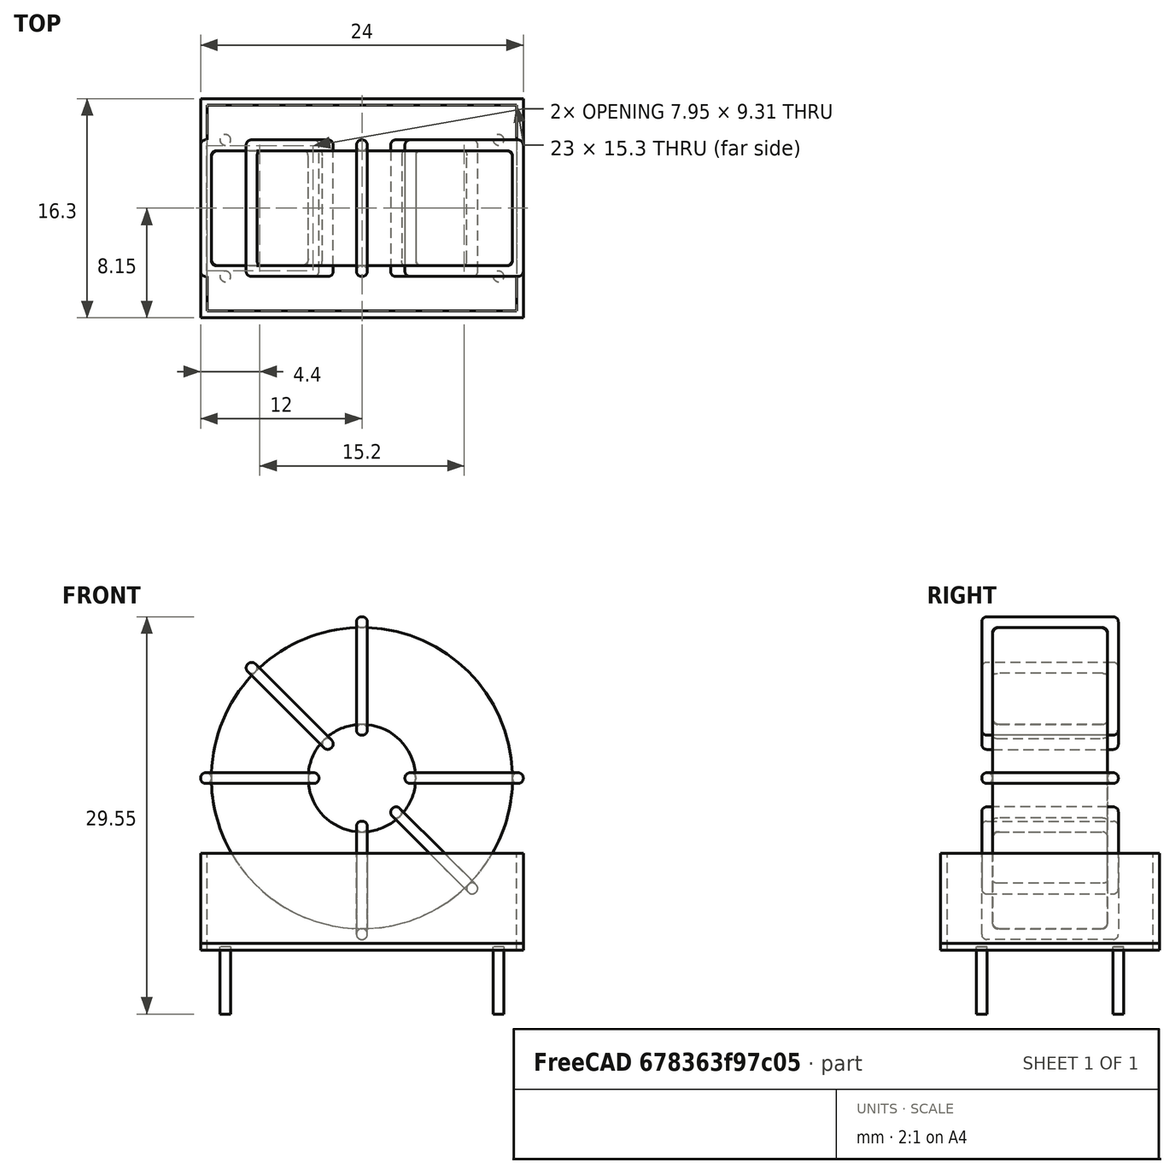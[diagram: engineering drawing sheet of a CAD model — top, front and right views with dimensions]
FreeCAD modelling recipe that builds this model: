
FCSTD DOCUMENT  (FreeCAD 0.16R6703 (Git))
Label: L_Radial_round_toroid_vertical_box_4pin_master
License: All rights reserved
LicenseURL: http://en.wikipedia.org/wiki/All_rights_reserved
objects: Sketcher::SketchObject×8, PartDesign::Pad×8, PartDesign::Fillet×5, Spreadsheet::Sheet×1
note: 29 computed .brp shape members not serialized (recipe doc carries the construction recipe); baked Part::Feature solids carry a one-line shape summary decoded from their .brp

FEATURE [Spreadsheet::Sheet] Spreadsheet  label="dimensions"
  cells = A1=Wx; B1(Wx)=24; C1(WW)=8; D1(iWx)=24; A2=Wy; B2(Wy)=10.16; D2(iWy)=16.3; A3=RM; B3(RMx)=10.16; C3(RMy)=20.32; A4=d_wire; B4(d_wire)=0.8; A5=H; B5(H)=31; A6=offsetx; B6(offsetx)=1.84
FEATURE [Sketcher::SketchObject] Sketch
  Placement = pos=(10.16,-5.08,0) rot=(1,0,0;1.5708rad)
  expr: Placement.Base.x = Spreadsheet.RMy / 2
  expr: Constraints[4] = Spreadsheet.WW / 2
  expr: Placement.Base.y = -Spreadsheet.RMx / 2
  expr: Constraints[0] = Spreadsheet.Wx / 2 - Spreadsheet.d_wire
  expr: Constraints[2] = Spreadsheet.Wx / 2 + Spreadsheet.d_wire + 0.5
  sketch-geometry (2):
    g0: Circle CenterX=0 CenterY=13.3 CenterZ=0 NormalX=0 NormalY=0 NormalZ=1 Radius=11.2
    g1: Circle CenterX=0 CenterY=13.3 CenterZ=0 NormalX=0 NormalY=0 NormalZ=1 Radius=4
  constraints (5):
    c: Radius(g0) = 11.2
    c: DistanceX(g-1,g0) = 0
    c: DistanceY(g-1,g0) = 13.3
    c: Coincident(g1,g0)
    c: Radius(g1) = 4
FEATURE [PartDesign::Pad] Pad
  Length = 8.56
  Length2 = 100
  Midplane = true
  Placement = pos=(10.16,-5.08,0) rot=(1,0,0;1.5708rad)
  Sketch = -> Sketch
  Type = 0
  expr: Length = Spreadsheet.Wy - 2 * Spreadsheet.d_wire
FEATURE [Sketcher::SketchObject] Sketch001
  Placement = pos=(0,0,0.75) rot=(0,0,1;0rad)
  expr: Constraints[4] = Spreadsheet.RMy
  expr: Constraints[2] = -Spreadsheet.RMx
  expr: Constraints[1] = Spreadsheet.d_wire / 2
  sketch-geometry (4):
    g0: Circle CenterX=0 CenterY=0 CenterZ=0 NormalX=0 NormalY=0 NormalZ=1 Radius=0.4
    g1: Circle CenterX=20.32 CenterY=-10.16 CenterZ=0 NormalX=0 NormalY=0 NormalZ=1 Radius=0.4
    g2: Circle CenterX=0 CenterY=-10.16 CenterZ=0 NormalX=0 NormalY=0 NormalZ=1 Radius=0.4
    g3: Circle CenterX=20.32 CenterY=0 CenterZ=0 NormalX=0 NormalY=0 NormalZ=1 Radius=0.4
  constraints (11):
    c: Equal(g0,g1)
    c: Radius(g0) = 0.4
    c: DistanceY(g-1,g1) = -10.16
    c: Coincident(g0,g-1)
    c: DistanceX(g-1,g1) = 20.32
    c: PointOnObject(g2,g-2)
    c: DistanceY(g-1,g3) = 0
    c: DistanceY(g2,g1) = 0
    c: DistanceX(g3,g1) = 0
    c: Equal(g3,g2)
    c: Equal(g2,g1)
FEATURE [PartDesign::Pad] Pad001
  Length = 5
  Length2 = 0
  Placement = pos=(0,0,0.75) rot=(0,0,1;0rad)
  Reversed = true
  Sketch = -> Sketch001
  Type = 0
FEATURE [PartDesign::Fillet] Fillet
  Base = -> Pad [Edge6,Edge3,Edge2]
  Placement = pos=(10.16,-5.08,0) rot=(1,0,0;1.5708rad)
  Radius = 0.5
FEATURE [Sketcher::SketchObject] Sketch003
  Placement = pos=(10.16,0,13.3) rot=(1,0,0;3.14159rad)
  expr: Placement.Base.x = Spreadsheet.RMy / 2
  expr: Constraints[18] = Spreadsheet.d_wire
  expr: Constraints[16] = Spreadsheet.d_wire
  expr: Constraints[19] = Spreadsheet.d_wire
  expr: Constraints[17] = Spreadsheet.d_wire
  expr: Placement.Base.y = -1 * (Spreadsheet.RMx - Spreadsheet.Wy) / 2
  expr: Constraints[21] = (Spreadsheet.Wx - Spreadsheet.WW) / 2 - Spreadsheet.d_wire
  expr: Constraints[22] = Spreadsheet.Wx / 2 - Spreadsheet.d_wire
  expr: Constraints[43] = Spreadsheet.d_wire
  expr: Constraints[48] = Spreadsheet.Wx - Spreadsheet.d_wire * 2
  expr: Constraints[49] = Spreadsheet.Wy
  expr: Placement.Base.z = Spreadsheet.Wx / 2 + Spreadsheet.d_wire + 0.5
  sketch-geometry (16):
    g0: LineSegment StartX=-3.2 StartY=0 StartZ=0 EndX=-12 EndY=0 EndZ=0
    g1: LineSegment StartX=-12 StartY=0 StartZ=0 EndX=-12 EndY=10.16 EndZ=0
    g2: LineSegment StartX=-12 StartY=10.16 StartZ=0 EndX=-3.2 EndY=10.16 EndZ=0
    g3: LineSegment StartX=-3.2 StartY=10.16 StartZ=0 EndX=-3.2 EndY=0 EndZ=0
    g4: LineSegment StartX=-11.2 StartY=9.36 StartZ=0 EndX=-4 EndY=9.36 EndZ=0
    g5: LineSegment StartX=-4 StartY=9.36 StartZ=0 EndX=-4 EndY=0.8 EndZ=0
    g6: LineSegment StartX=-4 StartY=0.8 StartZ=0 EndX=-11.2 EndY=0.8 EndZ=0
    g7: LineSegment StartX=-11.2 StartY=0.8 StartZ=0 EndX=-11.2 EndY=9.36 EndZ=0
    g8: LineSegment StartX=3.2 StartY=10.16 StartZ=0 EndX=12 EndY=10.16 EndZ=0
    g9: LineSegment StartX=12 StartY=10.16 StartZ=0 EndX=12 EndY=0 EndZ=0
    g10: LineSegment StartX=12 StartY=0 StartZ=0 EndX=3.2 EndY=0 EndZ=0
    g11: LineSegment StartX=3.2 StartY=0 StartZ=0 EndX=3.2 EndY=10.16 EndZ=0
    g12: LineSegment StartX=4 StartY=9.36 StartZ=0 EndX=11.2 EndY=9.36 EndZ=0
    g13: LineSegment StartX=11.2 StartY=9.36 StartZ=0 EndX=11.2 EndY=0.8 EndZ=0
    g14: LineSegment StartX=11.2 StartY=0.8 StartZ=0 EndX=4 EndY=0.8 EndZ=0
    g15: LineSegment StartX=4 StartY=0.8 StartZ=0 EndX=4 EndY=9.36 EndZ=0
  constraints (50):
    c: Horizontal(g0)
    c: Coincident(g1,g0)
    c: Vertical(g1)
    c: Coincident(g2,g1)
    c: Horizontal(g2)
    c: Coincident(g3,g2)
    c: Coincident(g3,g0)
    c: Vertical(g3)
    c: Coincident(g4,g5)
    c: Coincident(g5,g6)
    c: Coincident(g6,g7)
    c: Coincident(g7,g4)
    c: Horizontal(g4)
    c: Horizontal(g6)
    c: Vertical(g5)
    c: Vertical(g7)
    c: DistanceX(g1,g4) = 0.8
    c: DistanceY(g4,g1) = 0.8
    c: DistanceX(g5,g0) = 0.8
    c: DistanceY(g0,g5) = 0.8
    c: DistanceY(g-1,g0) = 0
    c: DistanceX(g6,g6) = 7.2
    c: DistanceX(g6,g-1) = 11.2
    c: Coincident(g8,g9)
    c: Coincident(g9,g10)
    c: Coincident(g10,g11)
    c: Coincident(g11,g8)
    c: Horizontal(g8)
    c: Horizontal(g10)
    c: Vertical(g9)
    c: Vertical(g11)
    c: Coincident(g12,g13)
    c: Coincident(g13,g14)
    c: Coincident(g14,g15)
    c: Coincident(g15,g12)
    c: Horizontal(g12)
    c: Horizontal(g14)
    c: Vertical(g13)
    c: Vertical(g15)
    c: DistanceY(g8,g2) = 0
    c: DistanceY(g10,g0) = 0
    c: DistanceY(g14,g5) = 0
    c: DistanceY(g12,g4) = 0
    c: DistanceX(g8,g12) = 0.8
    c: Equal(g8,g2)
    c: Equal(g12,g4)
    c: Equal(g9,g1)
    c: Equal(g13,g7)
    c: DistanceX(g4,g12) = 22.4
    c: DistanceY(g0,g1) = 10.16
FEATURE [PartDesign::Pad] Pad002
  Length = 0.8
  Length2 = 100
  Midplane = true
  Placement = pos=(10.16,0,13.3) rot=(1,0,0;3.14159rad)
  Sketch = -> Sketch003
  Type = 0
  expr: Length = Spreadsheet.d_wire
FEATURE [PartDesign::Fillet] Fillet001
  Base = -> Pad002 [Edge38,Edge41,Edge42,Edge43,Edge29,Edge32,Edge33,Edge34,Edge25,Edge35,Edge36,Edge13,Edge14,Edge15,Edge16,Edge17,Edge18,Edge19,Edge1,Edge2,Edge3,Edge4,Edge5,Edge6,Edge7,Edge37,Edge39,Edge40,Edge20,Edge23,Edge24,Edge21,Edge22,Edge8,Edge9,Edge10,Edge11,Edge12,Edge26,Edge27,+8 more]
  Placement = pos=(10.16,0,13.3) rot=(1,0,0;3.14159rad)
  Radius = 0.376
  expr: Radius = Spreadsheet.d_wire * 0.47
FEATURE [Sketcher::SketchObject] Sketch004
  Placement = pos=(10.16,0,13.3) rot=(0.92388,0,0.382683;3.14159rad)
  expr: Placement.Base.x = Spreadsheet.RMy / 2
  expr: Constraints[18] = Spreadsheet.d_wire
  expr: Constraints[16] = Spreadsheet.d_wire
  expr: Constraints[19] = Spreadsheet.d_wire
  expr: Constraints[17] = Spreadsheet.d_wire
  expr: Placement.Base.y = -1 * (Spreadsheet.RMx - Spreadsheet.Wy) / 2
  expr: Constraints[21] = (Spreadsheet.Wx - Spreadsheet.WW) / 2 - Spreadsheet.d_wire
  expr: Constraints[22] = Spreadsheet.Wx / 2 - Spreadsheet.d_wire
  expr: Constraints[43] = Spreadsheet.d_wire
  expr: Constraints[48] = Spreadsheet.Wx - 2 * Spreadsheet.d_wire
  expr: Constraints[49] = Spreadsheet.Wy
  expr: Placement.Base.z = Spreadsheet.Wx / 2 + Spreadsheet.d_wire + 0.5
  sketch-geometry (16):
    g0: LineSegment StartX=-3.2 StartY=0 StartZ=0 EndX=-12 EndY=0 EndZ=0
    g1: LineSegment StartX=-12 StartY=0 StartZ=0 EndX=-12 EndY=10.16 EndZ=0
    g2: LineSegment StartX=-12 StartY=10.16 StartZ=0 EndX=-3.2 EndY=10.16 EndZ=0
    g3: LineSegment StartX=-3.2 StartY=10.16 StartZ=0 EndX=-3.2 EndY=0 EndZ=0
    g4: LineSegment StartX=-11.2 StartY=9.36 StartZ=0 EndX=-4 EndY=9.36 EndZ=0
    g5: LineSegment StartX=-4 StartY=9.36 StartZ=0 EndX=-4 EndY=0.8 EndZ=0
    g6: LineSegment StartX=-4 StartY=0.8 StartZ=0 EndX=-11.2 EndY=0.8 EndZ=0
    g7: LineSegment StartX=-11.2 StartY=0.8 StartZ=0 EndX=-11.2 EndY=9.36 EndZ=0
    g8: LineSegment StartX=3.2 StartY=10.16 StartZ=0 EndX=12 EndY=10.16 EndZ=0
    g9: LineSegment StartX=12 StartY=10.16 StartZ=0 EndX=12 EndY=0 EndZ=0
    g10: LineSegment StartX=12 StartY=0 StartZ=0 EndX=3.2 EndY=0 EndZ=0
    g11: LineSegment StartX=3.2 StartY=0 StartZ=0 EndX=3.2 EndY=10.16 EndZ=0
    g12: LineSegment StartX=4 StartY=9.36 StartZ=0 EndX=11.2 EndY=9.36 EndZ=0
    g13: LineSegment StartX=11.2 StartY=9.36 StartZ=0 EndX=11.2 EndY=0.8 EndZ=0
    g14: LineSegment StartX=11.2 StartY=0.8 StartZ=0 EndX=4 EndY=0.8 EndZ=0
    g15: LineSegment StartX=4 StartY=0.8 StartZ=0 EndX=4 EndY=9.36 EndZ=0
  constraints (50):
    c: Horizontal(g0)
    c: Coincident(g1,g0)
    c: Vertical(g1)
    c: Coincident(g2,g1)
    c: Horizontal(g2)
    c: Coincident(g3,g2)
    c: Coincident(g3,g0)
    c: Vertical(g3)
    c: Coincident(g4,g5)
    c: Coincident(g5,g6)
    c: Coincident(g6,g7)
    c: Coincident(g7,g4)
    c: Horizontal(g4)
    c: Horizontal(g6)
    c: Vertical(g5)
    c: Vertical(g7)
    c: DistanceX(g1,g4) = 0.8
    c: DistanceY(g4,g1) = 0.8
    c: DistanceX(g5,g0) = 0.8
    c: DistanceY(g0,g5) = 0.8
    c: DistanceY(g-1,g0) = 0
    c: DistanceX(g6,g6) = 7.2
    c: DistanceX(g6,g-1) = 11.2
    c: Coincident(g8,g9)
    c: Coincident(g9,g10)
    c: Coincident(g10,g11)
    c: Coincident(g11,g8)
    c: Horizontal(g8)
    c: Horizontal(g10)
    c: Vertical(g9)
    c: Vertical(g11)
    c: Coincident(g12,g13)
    c: Coincident(g13,g14)
    c: Coincident(g14,g15)
    c: Coincident(g15,g12)
    c: Horizontal(g12)
    c: Horizontal(g14)
    c: Vertical(g13)
    c: Vertical(g15)
    c: DistanceY(g8,g2) = 0
    c: DistanceY(g10,g0) = 0
    c: DistanceY(g14,g5) = 0
    c: DistanceY(g12,g4) = 0
    c: DistanceX(g8,g12) = 0.8
    c: Equal(g8,g2)
    c: Equal(g12,g4)
    c: Equal(g9,g1)
    c: Equal(g13,g7)
    c: DistanceX(g4,g12) = 22.4
    c: DistanceY(g0,g1) = 10.16
FEATURE [PartDesign::Pad] Pad003
  Length = 0.8
  Length2 = 100
  Midplane = true
  Placement = pos=(10.16,0,13.3) rot=(0.92388,0,0.382683;3.14159rad)
  Sketch = -> Sketch004
  Type = 0
  expr: Length = Spreadsheet.d_wire
FEATURE [PartDesign::Fillet] Fillet002
  Base = -> Pad003 [Edge38,Edge41,Edge42,Edge43,Edge29,Edge32,Edge33,Edge34,Edge25,Edge35,Edge36,Edge13,Edge14,Edge15,Edge16,Edge17,Edge18,Edge19,Edge1,Edge2,Edge3,Edge4,Edge5,Edge6,Edge7,Edge37,Edge39,Edge40,Edge20,Edge23,Edge24,Edge21,Edge22,Edge8,Edge9,Edge10,Edge11,Edge12,Edge26,Edge27,+8 more]
  Placement = pos=(10.16,0,13.3) rot=(0.92388,0,0.382683;3.14159rad)
  Radius = 0.376
  expr: Radius = Spreadsheet.d_wire * 0.47
FEATURE [Sketcher::SketchObject] Sketch005
  Placement = pos=(10.16,0,13.3) rot=(0.92388,0,-0.382683;3.14159rad)
  expr: Placement.Base.x = Spreadsheet.RMy / 2
  expr: Constraints[18] = Spreadsheet.d_wire
  expr: Constraints[16] = Spreadsheet.d_wire
  expr: Constraints[19] = Spreadsheet.d_wire
  expr: Constraints[17] = Spreadsheet.d_wire
  expr: Placement.Base.y = -1 * (Spreadsheet.RMx - Spreadsheet.Wy) / 2
  expr: Constraints[21] = (Spreadsheet.Wx - Spreadsheet.WW) / 2 - Spreadsheet.d_wire
  expr: Constraints[22] = Spreadsheet.Wx / 2 - Spreadsheet.d_wire
  expr: Constraints[43] = Spreadsheet.d_wire
  expr: Constraints[48] = Spreadsheet.Wx - 2 * Spreadsheet.d_wire
  expr: Constraints[49] = Spreadsheet.Wy
  expr: Placement.Base.z = Spreadsheet.Wx / 2 + Spreadsheet.d_wire + 0.5
  sketch-geometry (16):
    g0: LineSegment StartX=-3.2 StartY=0 StartZ=0 EndX=-12 EndY=0 EndZ=0
    g1: LineSegment StartX=-12 StartY=0 StartZ=0 EndX=-12 EndY=10.16 EndZ=0
    g2: LineSegment StartX=-12 StartY=10.16 StartZ=0 EndX=-3.2 EndY=10.16 EndZ=0
    g3: LineSegment StartX=-3.2 StartY=10.16 StartZ=0 EndX=-3.2 EndY=0 EndZ=0
    g4: LineSegment StartX=-11.2 StartY=9.36 StartZ=0 EndX=-4 EndY=9.36 EndZ=0
    g5: LineSegment StartX=-4 StartY=9.36 StartZ=0 EndX=-4 EndY=0.8 EndZ=0
    g6: LineSegment StartX=-4 StartY=0.8 StartZ=0 EndX=-11.2 EndY=0.8 EndZ=0
    g7: LineSegment StartX=-11.2 StartY=0.8 StartZ=0 EndX=-11.2 EndY=9.36 EndZ=0
    g8: LineSegment StartX=3.2 StartY=10.16 StartZ=0 EndX=12 EndY=10.16 EndZ=0
    g9: LineSegment StartX=12 StartY=10.16 StartZ=0 EndX=12 EndY=0 EndZ=0
    g10: LineSegment StartX=12 StartY=0 StartZ=0 EndX=3.2 EndY=0 EndZ=0
    g11: LineSegment StartX=3.2 StartY=0 StartZ=0 EndX=3.2 EndY=10.16 EndZ=0
    g12: LineSegment StartX=4 StartY=9.36 StartZ=0 EndX=11.2 EndY=9.36 EndZ=0
    g13: LineSegment StartX=11.2 StartY=9.36 StartZ=0 EndX=11.2 EndY=0.8 EndZ=0
    g14: LineSegment StartX=11.2 StartY=0.8 StartZ=0 EndX=4 EndY=0.8 EndZ=0
    g15: LineSegment StartX=4 StartY=0.8 StartZ=0 EndX=4 EndY=9.36 EndZ=0
  constraints (50):
    c: Horizontal(g0)
    c: Coincident(g1,g0)
    c: Vertical(g1)
    c: Coincident(g2,g1)
    c: Horizontal(g2)
    c: Coincident(g3,g2)
    c: Coincident(g3,g0)
    c: Vertical(g3)
    c: Coincident(g4,g5)
    c: Coincident(g5,g6)
    c: Coincident(g6,g7)
    c: Coincident(g7,g4)
    c: Horizontal(g4)
    c: Horizontal(g6)
    c: Vertical(g5)
    c: Vertical(g7)
    c: DistanceX(g1,g4) = 0.8
    c: DistanceY(g4,g1) = 0.8
    c: DistanceX(g5,g0) = 0.8
    c: DistanceY(g0,g5) = 0.8
    c: DistanceY(g-1,g0) = 0
    c: DistanceX(g6,g6) = 7.2
    c: DistanceX(g6,g-1) = 11.2
    c: Coincident(g8,g9)
    c: Coincident(g9,g10)
    c: Coincident(g10,g11)
    c: Coincident(g11,g8)
    c: Horizontal(g8)
    c: Horizontal(g10)
    c: Vertical(g9)
    c: Vertical(g11)
    c: Coincident(g12,g13)
    c: Coincident(g13,g14)
    c: Coincident(g14,g15)
    c: Coincident(g15,g12)
    c: Horizontal(g12)
    c: Horizontal(g14)
    c: Vertical(g13)
    c: Vertical(g15)
    c: DistanceY(g8,g2) = 0
    c: DistanceY(g10,g0) = 0
    c: DistanceY(g14,g5) = 0
    c: DistanceY(g12,g4) = 0
    c: DistanceX(g8,g12) = 0.8
    c: Equal(g8,g2)
    c: Equal(g12,g4)
    c: Equal(g9,g1)
    c: Equal(g13,g7)
    c: DistanceX(g4,g12) = 22.4
    c: DistanceY(g0,g1) = 10.16
FEATURE [PartDesign::Pad] Pad004
  Length = 0.8
  Length2 = 100
  Midplane = true
  Placement = pos=(10.16,0,13.3) rot=(0.92388,0,-0.382683;3.14159rad)
  Sketch = -> Sketch005
  Type = 0
  expr: Length = Spreadsheet.d_wire
FEATURE [PartDesign::Fillet] Fillet003
  Base = -> Pad004 [Edge38,Edge41,Edge42,Edge43,Edge29,Edge32,Edge33,Edge34,Edge25,Edge35,Edge36,Edge13,Edge14,Edge15,Edge16,Edge17,Edge18,Edge19,Edge1,Edge2,Edge3,Edge4,Edge5,Edge6,Edge7,Edge37,Edge39,Edge40,Edge20,Edge23,Edge24,Edge21,Edge22,Edge8,Edge9,Edge10,Edge11,Edge12,Edge26,Edge27,+8 more]
  Placement = pos=(10.16,0,13.3) rot=(0.92388,0,-0.382683;3.14159rad)
  Radius = 0.376
  expr: Radius = Spreadsheet.d_wire * 0.47
FEATURE [Sketcher::SketchObject] Sketch006
  Placement = pos=(10.16,0,13.3) rot=(0.707107,0,0.707107;3.14159rad)
  expr: Placement.Base.x = Spreadsheet.RMy / 2
  expr: Constraints[18] = Spreadsheet.d_wire
  expr: Constraints[16] = Spreadsheet.d_wire
  expr: Constraints[19] = Spreadsheet.d_wire
  expr: Constraints[17] = Spreadsheet.d_wire
  expr: Placement.Base.y = -1 * (Spreadsheet.RMx - Spreadsheet.Wy) / 2
  expr: Constraints[21] = (Spreadsheet.Wx - Spreadsheet.WW) / 2 - Spreadsheet.d_wire
  expr: Constraints[22] = Spreadsheet.Wx / 2 - Spreadsheet.d_wire
  expr: Constraints[43] = Spreadsheet.d_wire
  expr: Constraints[48] = Spreadsheet.Wx - Spreadsheet.d_wire * 2
  expr: Constraints[49] = Spreadsheet.Wy
  expr: Placement.Base.z = Spreadsheet.Wx / 2 + Spreadsheet.d_wire + 0.5
  sketch-geometry (16):
    g0: LineSegment StartX=-3.2 StartY=0 StartZ=0 EndX=-12 EndY=0 EndZ=0
    g1: LineSegment StartX=-12 StartY=0 StartZ=0 EndX=-12 EndY=10.16 EndZ=0
    g2: LineSegment StartX=-12 StartY=10.16 StartZ=0 EndX=-3.2 EndY=10.16 EndZ=0
    g3: LineSegment StartX=-3.2 StartY=10.16 StartZ=0 EndX=-3.2 EndY=0 EndZ=0
    g4: LineSegment StartX=-11.2 StartY=9.36 StartZ=0 EndX=-4 EndY=9.36 EndZ=0
    g5: LineSegment StartX=-4 StartY=9.36 StartZ=0 EndX=-4 EndY=0.8 EndZ=0
    g6: LineSegment StartX=-4 StartY=0.8 StartZ=0 EndX=-11.2 EndY=0.8 EndZ=0
    g7: LineSegment StartX=-11.2 StartY=0.8 StartZ=0 EndX=-11.2 EndY=9.36 EndZ=0
    g8: LineSegment StartX=3.2 StartY=10.16 StartZ=0 EndX=12 EndY=10.16 EndZ=0
    g9: LineSegment StartX=12 StartY=10.16 StartZ=0 EndX=12 EndY=0 EndZ=0
    g10: LineSegment StartX=12 StartY=0 StartZ=0 EndX=3.2 EndY=0 EndZ=0
    g11: LineSegment StartX=3.2 StartY=0 StartZ=0 EndX=3.2 EndY=10.16 EndZ=0
    g12: LineSegment StartX=4 StartY=9.36 StartZ=0 EndX=11.2 EndY=9.36 EndZ=0
    g13: LineSegment StartX=11.2 StartY=9.36 StartZ=0 EndX=11.2 EndY=0.8 EndZ=0
    g14: LineSegment StartX=11.2 StartY=0.8 StartZ=0 EndX=4 EndY=0.8 EndZ=0
    g15: LineSegment StartX=4 StartY=0.8 StartZ=0 EndX=4 EndY=9.36 EndZ=0
  constraints (50):
    c: Horizontal(g0)
    c: Coincident(g1,g0)
    c: Vertical(g1)
    c: Coincident(g2,g1)
    c: Horizontal(g2)
    c: Coincident(g3,g2)
    c: Coincident(g3,g0)
    c: Vertical(g3)
    c: Coincident(g4,g5)
    c: Coincident(g5,g6)
    c: Coincident(g6,g7)
    c: Coincident(g7,g4)
    c: Horizontal(g4)
    c: Horizontal(g6)
    c: Vertical(g5)
    c: Vertical(g7)
    c: DistanceX(g1,g4) = 0.8
    c: DistanceY(g4,g1) = 0.8
    c: DistanceX(g5,g0) = 0.8
    c: DistanceY(g0,g5) = 0.8
    c: DistanceY(g-1,g0) = 0
    c: DistanceX(g6,g6) = 7.2
    c: DistanceX(g6,g-1) = 11.2
    c: Coincident(g8,g9)
    c: Coincident(g9,g10)
    c: Coincident(g10,g11)
    c: Coincident(g11,g8)
    c: Horizontal(g8)
    c: Horizontal(g10)
    c: Vertical(g9)
    c: Vertical(g11)
    c: Coincident(g12,g13)
    c: Coincident(g13,g14)
    c: Coincident(g14,g15)
    c: Coincident(g15,g12)
    c: Horizontal(g12)
    c: Horizontal(g14)
    c: Vertical(g13)
    c: Vertical(g15)
    c: DistanceY(g8,g2) = 0
    c: DistanceY(g10,g0) = 0
    c: DistanceY(g14,g5) = 0
    c: DistanceY(g12,g4) = 0
    c: DistanceX(g8,g12) = 0.8
    c: Equal(g8,g2)
    c: Equal(g12,g4)
    c: Equal(g9,g1)
    c: Equal(g13,g7)
    c: DistanceX(g4,g12) = 22.4
    c: DistanceY(g0,g1) = 10.16
FEATURE [PartDesign::Pad] Pad005
  Length = 0.8
  Length2 = 100
  Midplane = true
  Placement = pos=(10.16,0,13.3) rot=(0.707107,0,0.707107;3.14159rad)
  Sketch = -> Sketch006
  Type = 0
  expr: Length = Spreadsheet.d_wire
FEATURE [PartDesign::Fillet] Fillet004
  Base = -> Pad005 [Edge38,Edge41,Edge42,Edge43,Edge29,Edge32,Edge33,Edge34,Edge25,Edge35,Edge36,Edge13,Edge14,Edge15,Edge16,Edge17,Edge18,Edge19,Edge1,Edge2,Edge3,Edge4,Edge5,Edge6,Edge7,Edge37,Edge39,Edge40,Edge20,Edge23,Edge24,Edge21,Edge22,Edge8,Edge9,Edge10,Edge11,Edge12,Edge26,Edge27,+8 more]
  Placement = pos=(10.16,0,13.3) rot=(0.707107,0,0.707107;3.14159rad)
  Radius = 0.376
  expr: Radius = Spreadsheet.d_wire * 0.47
FEATURE [Sketcher::SketchObject] Sketch007
  Placement = pos=(10.16,0,0.5) rot=(0,0,1;0rad)
  expr: Placement.Base.x = Spreadsheet.RMy / 2
  expr: Placement.Base.z = 0.5
  expr: Constraints[11] = Spreadsheet.iWx / 2
  expr: Constraints[10] = (Spreadsheet.iWy - Spreadsheet.RMx) / 2
  expr: Constraints[9] = Spreadsheet.iWy
  expr: Constraints[8] = Spreadsheet.iWx
  sketch-geometry (4):
    g0: LineSegment StartX=-12 StartY=3.07 StartZ=0 EndX=12 EndY=3.07 EndZ=0
    g1: LineSegment StartX=12 StartY=3.07 StartZ=0 EndX=12 EndY=-13.23 EndZ=0
    g2: LineSegment StartX=12 StartY=-13.23 StartZ=0 EndX=-12 EndY=-13.23 EndZ=0
    g3: LineSegment StartX=-12 StartY=-13.23 StartZ=0 EndX=-12 EndY=3.07 EndZ=0
  constraints (12):
    c: Coincident(g0,g1)
    c: Coincident(g1,g2)
    c: Coincident(g2,g3)
    c: Coincident(g3,g0)
    c: Horizontal(g0)
    c: Horizontal(g2)
    c: Vertical(g1)
    c: Vertical(g3)
    c: DistanceX(g0,g0) = 24
    c: DistanceY(g3,g3) = 16.3
    c: DistanceY(g-1,g0) = 3.07
    c: DistanceX(g0,g-1) = 12
FEATURE [PartDesign::Pad] Pad006
  Length = 0.5
  Length2 = 100
  Placement = pos=(10.16,0,0.5) rot=(0,0,1;0rad)
  Sketch = -> Sketch007
  Type = 0
FEATURE [Sketcher::SketchObject] Sketch008
  Placement = pos=(10.16,0,0.5) rot=(0,0,1;0rad)
  expr: Placement.Base.x = Spreadsheet.RMy / 2
  expr: Constraints[8] = Spreadsheet.iWx
  expr: Constraints[9] = Spreadsheet.iWy
  expr: Constraints[10] = (Spreadsheet.iWy - Spreadsheet.RMx) / 2
  expr: Placement.Base.z = 0.5
  expr: Constraints[21] = 0.5
  expr: Constraints[11] = Spreadsheet.iWx / 2
  sketch-geometry (8):
    g0: LineSegment StartX=-12 StartY=3.07 StartZ=0 EndX=12 EndY=3.07 EndZ=0
    g1: LineSegment StartX=12 StartY=3.07 StartZ=0 EndX=12 EndY=-13.23 EndZ=0
    g2: LineSegment StartX=12 StartY=-13.23 StartZ=0 EndX=-12 EndY=-13.23 EndZ=0
    g3: LineSegment StartX=-12 StartY=-13.23 StartZ=0 EndX=-12 EndY=3.07 EndZ=0
    g4: LineSegment StartX=-11.5 StartY=2.57 StartZ=0 EndX=11.5 EndY=2.57 EndZ=0
    g5: LineSegment StartX=11.5 StartY=2.57 StartZ=0 EndX=11.5 EndY=-12.73 EndZ=0
    g6: LineSegment StartX=11.5 StartY=-12.73 StartZ=0 EndX=-11.5 EndY=-12.73 EndZ=0
    g7: LineSegment StartX=-11.5 StartY=-12.73 StartZ=0 EndX=-11.5 EndY=2.57 EndZ=0
  constraints (24):
    c: Coincident(g0,g1)
    c: Coincident(g1,g2)
    c: Coincident(g2,g3)
    c: Coincident(g3,g0)
    c: Horizontal(g0)
    c: Horizontal(g2)
    c: Vertical(g1)
    c: Vertical(g3)
    c: DistanceX(g0,g0) = 24
    c: DistanceY(g3,g3) = 16.3
    c: DistanceY(g-1,g0) = 3.07
    c: DistanceX(g0,g-1) = 12
    c: Coincident(g4,g5)
    c: Coincident(g5,g6)
    c: Coincident(g6,g7)
    c: Coincident(g7,g4)
    c: Horizontal(g4)
    c: Horizontal(g6)
    c: Vertical(g5)
    c: Vertical(g7)
    c: DistanceX(g5,g1) = 0.5
    c: DistanceY(g1,g5) = 0.5
    c: DistanceX(g0,g4) = 0.5
    c: DistanceY(g4,g0) = 0.5
FEATURE [PartDesign::Pad] Pad007
  Length = 7.2
  Length2 = 100
  Placement = pos=(10.16,0,0.5) rot=(0,0,1;0rad)
  Sketch = -> Sketch008
  Type = 0
  expr: Length = Spreadsheet.Wx * 0.3
